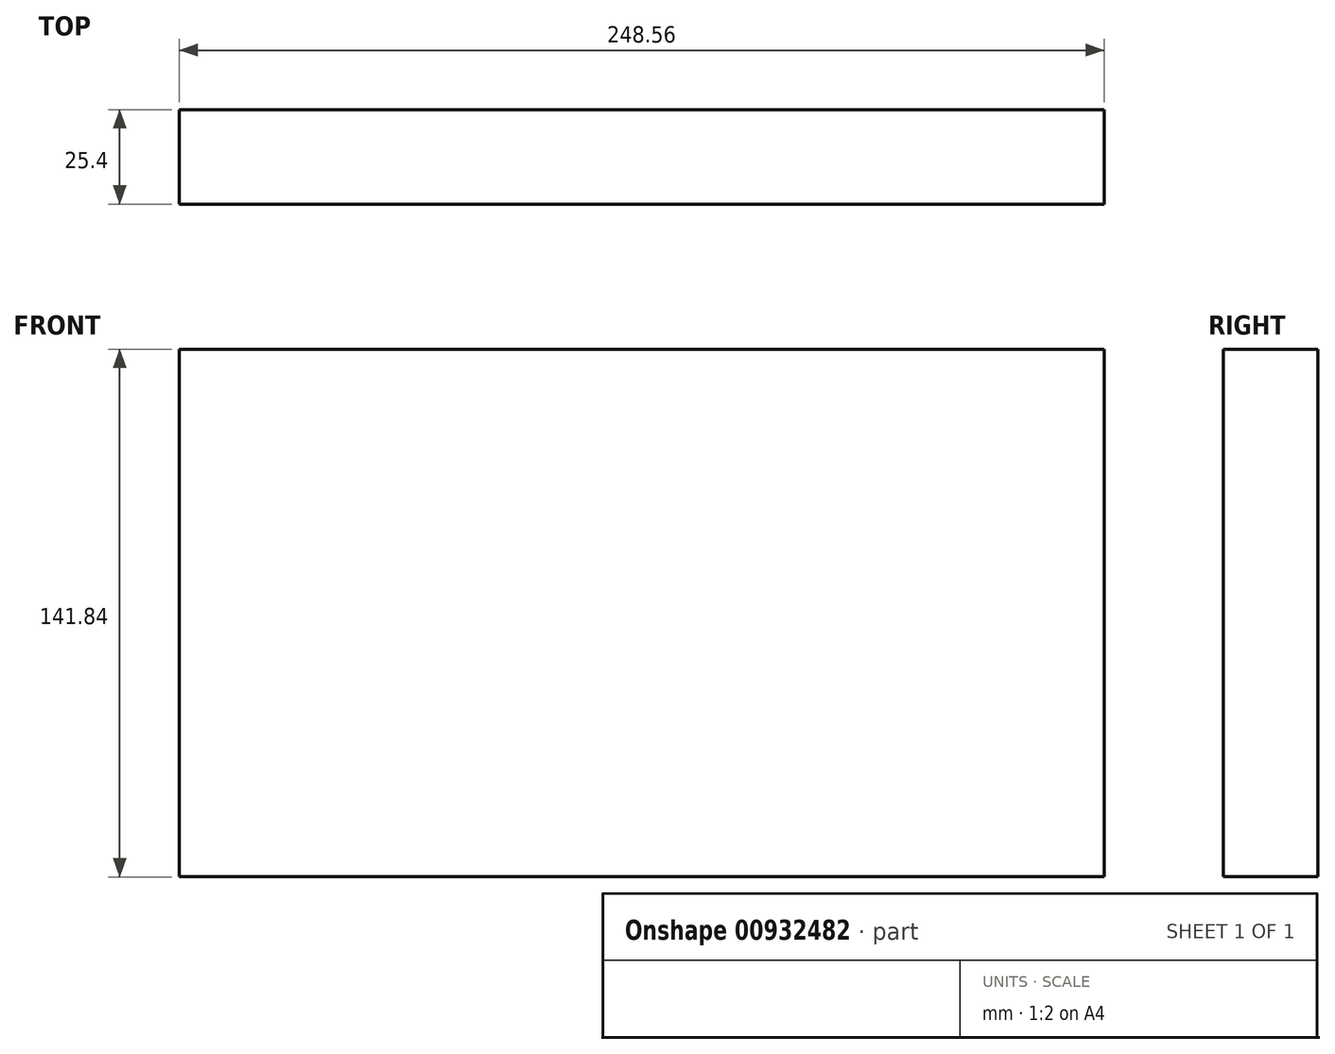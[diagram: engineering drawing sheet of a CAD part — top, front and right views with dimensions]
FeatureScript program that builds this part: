
annotation { "Feature Type Name" : "Feature", "Feature Type Description" : "" }
export const myFeature = defineFeature(function(context is Context, id is Id, definition is map)
    precondition{}
    {
        {
            var Q0;
            Q0=qCreatedBy(makeId("Front.planeOp"),FACE);
            var sketch = newSketch(context, id + "F0", { "sketchPlane" : qUnion([Q0])});
            skLineSegment(sketch, "E0.bottom", {"start": v(-115.4, 60.03) * mm, "end": v(133.16, 60.03) * mm});
            skLineSegment(sketch, "E0.top", {"start": v(-115.4, -81.8) * mm, "end": v(133.16, -81.8) * mm});
            skLineSegment(sketch, "E0.left", {"start": v(-115.4, 60.03) * mm, "end": v(-115.4, -81.8) * mm});
            skLineSegment(sketch, "E0.right", {"start": v(133.16, 60.03) * mm, "end": v(133.16, -81.8) * mm});
            skSolve(sketch);
        }
        {
            var Q0;
            Q0=makeQuery(id+"F0.imprint","IMPRINT",FACE,{"disambiguationData":[TD([[makeQuery(id+"F0.imprint","IMPRINT",EDGE,{"derivedFrom":sQuery(id+"F0.wireOp",EDGE,"E0.bottom")}),-1.0]])]});
            extrude(context, id + "F1", {"entities" : qUnion([Q0]), "endBound" : BoundingType.SYMMETRIC, "depth" : 25.4 * mm, "offsetDistance" : 25.4 * mm});
        }
    });
